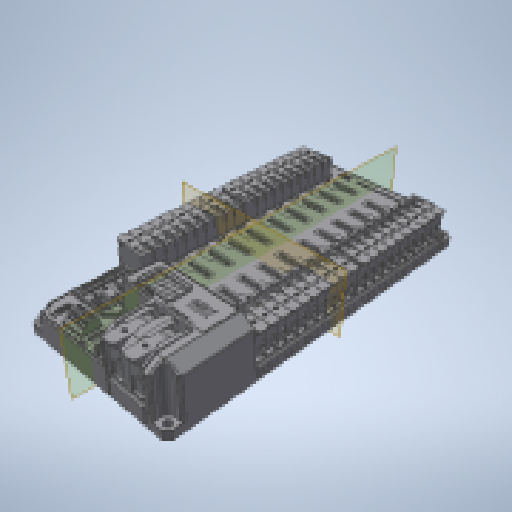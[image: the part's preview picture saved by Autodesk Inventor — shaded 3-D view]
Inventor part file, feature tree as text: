
AUTODESK INVENTOR PART (.ipt)
format: ipt  version: 2023.3 (Build 273359000, 359)  size: 30,591,488 bytes
history: native  units: mm (DEFAULTED — no unit token found)
features: other x402, plane x2
ambient origin geometry x8: Origin, YZ Plane, XZ Plane, XY Plane, X Axis, Y Axis, Z Axis, Center Point
bodies: Solid1 (feature_tree), Solid2 (feature_tree), Solid3 (feature_tree), Solid4 (feature_tree), Solid5 (feature_tree), Solid6 (feature_tree), Solid7 (feature_tree), Solid8 (feature_tree), Solid9 (feature_tree), Solid10 (feature_tree), Solid11 (feature_tree), Solid12 (feature_tree), Solid13 (feature_tree), Solid14 (feature_tree), Solid15 (feature_tree), Solid16 (feature_tree), Solid17 (feature_tree), Solid18 (feature_tree), Solid19 (feature_tree), Solid20 (feature_tree), Solid21 (feature_tree), Solid22 (feature_tree), Solid23 (feature_tree), Solid24 (feature_tree), Solid25 (feature_tree), Solid26 (feature_tree), Solid27 (feature_tree), Solid28 (feature_tree), Solid29 (feature_tree), Solid30 (feature_tree), Solid31 (feature_tree), Solid32 (feature_tree), Solid33 (feature_tree), Solid34 (feature_tree), Solid35 (feature_tree), Solid36 (feature_tree), Solid37 (feature_tree), Solid38 (feature_tree), Solid39 (feature_tree), Solid40 (feature_tree), Solid41 (feature_tree), Solid42 (feature_tree), Solid43 (feature_tree), Solid44 (feature_tree), Solid45 (feature_tree), Solid46 (feature_tree), Solid47 (feature_tree), Solid48 (feature_tree), Solid49 (feature_tree), Solid50 (feature_tree), Solid51 (feature_tree), Solid52 (feature_tree), Solid53 (feature_tree), Solid54 (feature_tree), Solid55 (feature_tree), Solid56 (feature_tree), Solid57 (feature_tree), Solid58 (feature_tree), Solid59 (feature_tree), Solid60 (feature_tree), Solid61 (feature_tree), Solid62 (feature_tree), Solid63 (feature_tree), Solid64 (feature_tree), Solid65 (feature_tree), Solid66 (feature_tree), Solid67 (feature_tree), Solid68 (feature_tree), Solid69 (feature_tree), Solid70 (feature_tree), Solid71 (feature_tree), Solid72 (feature_tree), Solid73 (feature_tree), Solid74 (feature_tree), Solid75 (feature_tree), Solid76 (feature_tree), Solid77 (feature_tree), Solid78 (feature_tree), Solid79 (feature_tree), Solid80 (feature_tree), Solid81 (feature_tree), Solid82 (feature_tree), Solid83 (feature_tree), Solid84 (feature_tree), Solid85 (feature_tree), Solid86 (feature_tree), Solid87 (feature_tree), Solid88 (feature_tree), Solid89 (feature_tree), Solid90 (feature_tree), Solid91 (feature_tree), Solid92 (feature_tree), Solid93 (feature_tree), Solid94 (feature_tree), Solid95 (feature_tree), Solid96 (feature_tree), Solid97 (feature_tree), Solid98 (feature_tree), Solid99 (feature_tree), Solid100 (feature_tree), Solid101 (feature_tree), Solid102 (feature_tree), Solid103 (feature_tree), Solid104 (feature_tree), Solid105 (feature_tree), Solid106 (feature_tree), Solid107 (feature_tree), Solid108 (feature_tree), Solid109 (feature_tree), Solid110 (feature_tree), Solid111 (feature_tree), Solid112 (feature_tree), Solid113 (feature_tree), Solid114 (feature_tree), Solid115 (feature_tree), Solid116 (feature_tree), Solid117 (feature_tree), Solid118 (feature_tree), Solid119 (feature_tree), Solid120 (feature_tree), Solid121 (feature_tree), Solid122 (feature_tree), Solid123 (feature_tree), Solid124 (feature_tree), Solid125 (feature_tree), Solid126 (feature_tree), Solid127 (feature_tree), Solid128 (feature_tree), Solid129 (feature_tree), Solid130 (feature_tree), Solid131 (feature_tree), Solid132 (feature_tree), Solid133 (feature_tree), Solid134 (feature_tree), Solid135 (feature_tree), Solid136 (feature_tree), Solid137 (feature_tree), Solid138 (feature_tree), Solid139 (feature_tree), Solid140 (feature_tree), Solid141 (feature_tree), Solid142 (feature_tree), Solid143 (feature_tree), Solid144 (feature_tree), Solid145 (feature_tree), Solid146 (feature_tree), Solid147 (feature_tree), Solid148 (feature_tree), Solid149 (feature_tree), Solid150 (feature_tree), Solid151 (feature_tree), Solid152 (feature_tree), Solid153 (feature_tree), Solid154 (feature_tree), Solid155 (feature_tree), Solid156 (feature_tree), Solid157 (feature_tree), Solid158 (feature_tree), Solid159 (feature_tree), Solid160 (feature_tree), Solid161 (feature_tree), Solid162 (feature_tree), Solid163 (feature_tree), Solid164 (feature_tree), Solid165 (feature_tree), Solid166 (feature_tree), Solid167 (feature_tree), Solid168 (feature_tree), Solid169 (feature_tree), Solid170 (feature_tree), Solid171 (feature_tree), Solid172 (feature_tree), Solid173 (feature_tree), Solid174 (feature_tree), Solid175 (feature_tree), Solid176 (feature_tree), Solid177 (feature_tree), Solid178 (feature_tree), Solid179 (feature_tree), Solid180 (feature_tree), Solid181 (feature_tree), Solid182 (feature_tree), Solid183 (feature_tree), Solid184 (feature_tree), Solid185 (feature_tree), Solid186 (feature_tree), Solid187 (feature_tree), Solid188 (feature_tree), Solid189 (feature_tree), Solid190 (feature_tree), Solid191 (feature_tree), Solid192 (feature_tree), Solid193 (feature_tree), Solid194 (feature_tree), Solid195 (feature_tree), Solid196 (feature_tree), Solid197 (feature_tree), Solid198 (feature_tree), Solid199 (feature_tree), Solid200 (feature_tree), Solid201 (feature_tree), Solid202 (feature_tree), Solid203 (feature_tree), Solid204 (feature_tree), Solid205 (feature_tree), Solid206 (feature_tree), Solid207 (feature_tree), Solid208 (feature_tree), Solid209 (feature_tree), Solid210 (feature_tree), Solid211 (feature_tree), Solid212 (feature_tree), Solid213 (feature_tree), Solid214 (feature_tree), Solid215 (feature_tree), Solid216 (feature_tree), Solid217 (feature_tree), Solid218 (feature_tree), Solid219 (feature_tree), Solid220 (feature_tree), Solid221 (feature_tree), Solid222 (feature_tree), Solid223 (feature_tree), Solid224 (feature_tree), Solid225 (feature_tree), Solid226 (feature_tree), Solid227 (feature_tree), Solid228 (feature_tree), Solid229 (feature_tree), Solid230 (feature_tree), Solid231 (feature_tree), Solid232 (feature_tree), Solid233 (feature_tree), Solid234 (feature_tree), Solid235 (feature_tree), Solid236 (feature_tree), Solid237 (feature_tree), Solid238 (feature_tree), Solid239 (feature_tree), Solid240 (feature_tree), Solid241 (feature_tree), Solid242 (feature_tree), Solid243 (feature_tree), Solid244 (feature_tree), Solid245 (feature_tree), Solid246 (feature_tree), Solid247 (feature_tree), Solid248 (feature_tree), Solid249 (feature_tree), Solid250 (feature_tree), Solid251 (feature_tree), Solid252 (feature_tree), Solid253 (feature_tree), Solid254 (feature_tree), Solid255 (feature_tree), Solid256 (feature_tree), Solid257 (feature_tree), Solid258 (feature_tree), Solid259 (feature_tree), Solid260 (feature_tree), Solid261 (feature_tree), Solid262 (feature_tree), Solid263 (feature_tree), Solid264 (feature_tree), Solid265 (feature_tree), Solid266 (feature_tree), Solid267 (feature_tree), Solid268 (feature_tree), Solid269 (feature_tree), Solid270 (feature_tree), Solid271 (feature_tree), Solid272 (feature_tree), Solid273 (feature_tree), Solid274 (feature_tree), Solid275 (feature_tree), Solid276 (feature_tree), Solid277 (feature_tree), Solid278 (feature_tree), Solid279 (feature_tree), Solid280 (feature_tree), Solid281 (feature_tree), Solid282 (feature_tree), Solid283 (feature_tree), Solid284 (feature_tree), Solid285 (feature_tree), Solid286 (feature_tree), Solid287 (feature_tree), Solid288 (feature_tree), Solid289 (feature_tree), Solid290 (feature_tree), Solid291 (feature_tree), Solid292 (feature_tree), Solid293 (feature_tree), Solid294 (feature_tree), Solid295 (feature_tree), Solid296 (feature_tree), Solid297 (feature_tree), Solid298 (feature_tree), Solid299 (feature_tree), Solid300 (feature_tree), Solid301 (feature_tree), Solid302 (feature_tree), Solid303 (feature_tree), Solid304 (feature_tree), Solid305 (feature_tree), Solid306 (feature_tree), Solid307 (feature_tree), Solid308 (feature_tree), Solid309 (feature_tree), Solid310 (feature_tree), Solid311 (feature_tree), Solid312 (feature_tree), Solid313 (feature_tree), Solid314 (feature_tree), Solid315 (feature_tree), Solid316 (feature_tree), Solid317 (feature_tree), Solid318 (feature_tree), Solid319 (feature_tree), Solid320 (feature_tree), Solid321 (feature_tree), Solid322 (feature_tree), Solid323 (feature_tree), Solid324 (feature_tree), Solid325 (feature_tree), Solid326 (feature_tree), Solid327 (feature_tree), Solid328 (feature_tree), Solid329 (feature_tree), Solid330 (feature_tree), Solid331 (feature_tree), Solid332 (feature_tree), Solid333 (feature_tree), Solid334 (feature_tree), Solid335 (feature_tree), Solid336 (feature_tree), Solid337 (feature_tree), Solid338 (feature_tree), Solid339 (feature_tree), Solid340 (feature_tree), Solid341 (feature_tree), Solid342 (feature_tree), Solid343 (feature_tree), Solid344 (feature_tree), Solid345 (feature_tree), Solid346 (feature_tree), Solid347 (feature_tree), Solid348 (feature_tree), Solid349 (feature_tree), Solid350 (feature_tree), Solid351 (feature_tree), Solid352 (feature_tree), Solid353 (feature_tree), Solid354 (feature_tree), Solid355 (feature_tree), Solid356 (feature_tree), Solid357 (feature_tree), Solid358 (feature_tree), Solid359 (feature_tree), Solid360 (feature_tree), Solid361 (feature_tree), Solid362 (feature_tree), Solid363 (feature_tree), Solid364 (feature_tree), Solid365 (feature_tree), Solid366 (feature_tree), Solid367 (feature_tree), Solid368 (feature_tree), Solid369 (feature_tree), Solid370 (feature_tree), Solid371 (feature_tree), Solid372 (feature_tree), Solid373 (feature_tree), Solid374 (feature_tree), Solid375 (feature_tree), Solid376 (feature_tree), Solid377 (feature_tree), Solid378 (feature_tree), Solid379 (feature_tree), Solid380 (feature_tree), Solid381 (feature_tree), Solid382 (feature_tree), Solid383 (feature_tree), Solid384 (feature_tree), Solid385 (feature_tree), Solid386 (feature_tree), Solid387 (feature_tree), Solid388 (feature_tree), Solid389 (feature_tree), Solid390 (feature_tree), Solid391 (feature_tree), Solid392 (feature_tree), Solid393 (feature_tree), Solid394 (feature_tree), Solid395 (feature_tree), Solid396 (feature_tree), Solid397 (feature_tree), Solid398 (feature_tree), Solid399 (feature_tree), Solid400 (feature_tree), Solid401 (feature_tree), Solid402 (feature_tree), Solid403 (feature_tree)
feature tree (404):
  plane  "Work Plane1"
  plane  "Work Plane2"
  other  "REV-11-1850-P01-1-solid1"
  other  "REV-11-1850-P02-1-solid1"
  other  "REV-11-1850-P02-1-solid2"
  other  "REV-11-1850-P02-1-solid3"
  other  "REV-11-1850-P02-1-solid4"
  other  "REV-11-1850-P02-1-solid5"
  other  "REV-11-1850-P02-1-solid6"
  other  "REV-11-1850-P02-1-solid7"
  other  "REV-11-1850-P02-1-solid8"
  other  "REV-11-1850-P02-1-solid9"
  other  "REV-11-1850-P02-1-solid10"
  other  "REV-11-1850-P02-1-solid11"
  other  "REV-11-1850-P02-1-solid12"
  other  "REV-11-1850-P02-1-solid13"
  other  "REV-11-1850-P02-1-solid14"
  other  "REV-11-1850-P02-1-solid15"
  other  "REV-11-1850-P02-1-solid16"
  other  "REV-11-1850-P02-1-solid17"
  other  "REV-11-1850-P02-1-solid18"
  other  "REV-11-1850-P02-1-solid19"
  other  "REV-11-1850-P02-1-solid20"
  other  "REV-11-1850-P02-1-solid21"
  other  "REV-11-1850-P02-1-solid22"
  other  "REV-11-1850-P02-1-solid23"
  other  "REV-11-1850-P02-1-solid24"
  other  "REV-11-1850-P02-1-solid25"
  other  "REV-11-1850-P02-1-solid26"
  other  "REV-11-1850-P02-1-solid27"
  other  "REV-11-1850-P02-1-solid28"
  other  "REV-11-1850-P02-1-solid29"
  other  "REV-11-1850-P02-1-solid30"
  other  "REV-11-1850-P02-1-solid31"
  other  "REV-11-1850-P02-1-solid32"
  other  "REV-11-1850-P02-1-solid33"
  other  "REV-11-1850-P03-1-solid1"
  other  "REV-11-1850-P03-1-solid2"
  other  "REV-11-1850-P03-1-solid3"
  other  "REV-11-1850-P03-1-solid4"
  other  "REV-11-1850-P03-1-solid5"
  other  "REV-11-1850-P03-1-solid6"
  other  "REV-11-1850-P03-1-solid7"
  other  "REV-11-1850-P03-1-solid8"
  other  "REV-11-1850-P03-1-solid9"
  other  "REV-11-1850-P03-1-solid10"
  other  "REV-11-1850-P03-1-solid11"
  other  "REV-11-1850-P03-1-solid12"
  other  "REV-11-1850-P03-1-solid13"
  other  "REV-11-1850-P03-1-solid14"
  other  "REV-11-1850-P03-1-solid15"
  other  "REV-11-1850-P03-1-solid16"
  other  "REV-11-1850-P03-1-solid17"
  other  "REV-11-1850-P03-1-solid18"
  other  "REV-11-1850-P03-1-solid19"
  other  "REV-11-1850-P03-1-solid20"
  other  "REV-11-1850-P03-1-solid21"
  other  "REV-11-1850-P03-1-solid22"
  other  "REV-11-1850-P03-1-solid23"
  other  "REV-11-1850-P03-1-solid24"
  other  "REV-11-1850-P03-1-solid25"
  other  "REV-11-1850-P03-1-solid26"
  other  "REV-11-1850-P03-1-solid27"
  other  "REV-11-1850-P03-1-solid28"
  other  "REV-11-1850-P03-1-solid29"
  other  "REV-11-1850-P03-1-solid30"
  other  "REV-11-1850-P03-1-solid31"
  other  "REV-11-1850-P03-1-solid32"
  other  "REV-11-1850-P03-1-solid33"
  other  "REV-11-1850-P03-1-solid34"
  other  "REV-11-1850-P03-1-solid35"
  other  "REV-11-1850-P03-1-solid36"
  other  "REV-11-1850-P03-1-solid37"
  other  "REV-11-1850-P03-1-solid38"
  other  "REV-11-1850-P03-1-solid39"
  other  "REV-11-1850-P03-1-solid40"
  other  "REV-11-1850-P04-1-solid1"
  other  "REV-11-1850-P04-1-solid2"
  other  "REV-11-1850-P04-1-solid3"
  other  "REV-11-1850-P04-1-solid4"
  other  "REV-11-1850-P04-1-solid5"
  other  "REV-11-1850-P04-1-solid6"
  other  "REV-11-1850-P04-1-solid7"
  other  "REV-11-1850-P04-1-solid8"
  other  "REV-11-1850-P04-1-solid9"
  other  "REV-11-1850-P04-1-solid10"
  other  "REV-11-1850-P04-1-solid11"
  other  "REV-11-1850-P04-1-solid12"
  other  "REV-11-1850-P04-1-solid13"
  other  "REV-11-1850-P04-1-solid14"
  other  "REV-11-1850-P04-1-solid15"
  other  "REV-11-1850-P04-1-solid16"
  other  "REV-11-1850-P04-1-solid17"
  other  "REV-11-1850-P04-1-solid18"
  other  "REV-11-1850-P04-1-solid19"
  other  "REV-11-1850-P04-1-solid20"
  other  "REV-11-1850-P04-1-solid21"
  other  "REV-11-1850-P04-1-solid22"
  other  "REV-11-1850-P04-1-solid23"
  other  "REV-11-1850-P04-1-solid24"
  other  "REV-11-1850-P04-1-solid25"
  other  "REV-11-1850-P04-1-solid26"
  other  "REV-11-1850-P04-1-solid27"
  other  "REV-11-1850-P04-1-solid28"
  other  "REV-11-1850-P04-1-solid29"
  other  "REV-11-1850-P04-1-solid30"
  other  "REV-11-1850-P04-1-solid31"
  other  "REV-11-1850-P04-1-solid32"
  other  "REV-11-1850-P04-1-solid33"
  other  "REV-11-1850-P04-1-solid34"
  other  "REV-11-1850-P04-1-solid35"
  other  "REV-11-1850-P04-1-solid36"
  other  "REV-11-1850-P04-1-solid37"
  other  "REV-11-1850-P04-1-solid38"
  other  "REV-11-1850-P04-1-solid39"
  other  "REV-11-1850-P04-1-solid40"
  other  "REV-11-1850-P04-1-solid41"
  other  "REV-11-1850-P04-1-solid42"
  other  "REV-11-1850-P04-1-solid43"
  other  "REV-11-1850-P04-1-solid44"
  other  "REV-11-1850-P04-1-solid45"
  other  "REV-11-1850-P04-1-solid46"
  other  "REV-11-1850-P04-1-solid47"
  other  "REV-11-1850-P04-1-solid48"
  other  "REV-11-1850-P04-1-solid49"
  other  "REV-11-1850-P04-1-solid50"
  other  "REV-11-1850-P04-1-solid51"
  other  "REV-11-1850-P04-1-solid52"
  other  "REV-11-1850-P04-1-solid53"
  other  "REV-11-1850-P04-1-solid54"
  other  "REV-11-1850-P04-1-solid55"
  other  "REV-11-1850-P04-1-solid56"
  other  "REV-11-1850-P04-1-solid57"
  other  "REV-11-1850-P04-1-solid58"
  other  "REV-11-1850-P04-1-solid59"
  other  "REV-11-1850-P04-1-solid60"
  other  "REV-11-1850-P04-1-solid61"
  other  "REV-11-1850-P04-1-solid62"
  other  "REV-11-1850-P04-1-solid63"
  other  "REV-11-1850-P04-1-solid64"
  other  "REV-11-1850-P04-1-solid65"
  other  "REV-11-1850-P04-1-solid66"
  other  "REV-11-1850-P04-1-solid67"
  other  "REV-11-1850-P04-1-solid68"
  other  "REV-11-1850-P04-1-solid69"
  other  "REV-11-1850-P04-1-solid70"
  other  "REV-11-1850-P04-1-solid71"
  other  "REV-11-1850-P04-1-solid72"
  other  "REV-11-1850-P04-1-solid73"
  other  "REV-11-1850-P04-1-solid74"
  other  "REV-11-1850-P04-1-solid75"
  other  "REV-11-1850-P04-1-solid76"
  other  "REV-11-1850-P04-1-solid77"
  other  "REV-11-1850-P04-1-solid78"
  other  "REV-11-1850-P04-1-solid79"
  other  "REV-11-1850-P04-1-solid80"
  other  "REV-11-1850-P04-1-solid81"
  other  "REV-11-1850-P04-1-solid82"
  other  "REV-11-1850-P04-1-solid83"
  other  "REV-11-1850-P04-1-solid84"
  other  "REV-11-1850-P04-1-solid85"
  other  "REV-11-1850-P04-1-solid86"
  other  "REV-11-1850-P04-1-solid87"
  other  "REV-11-1850-P04-1-solid88"
  other  "REV-11-1850-P04-1-solid89"
  other  "REV-11-1850-P04-1-solid90"
  other  "REV-11-1850-P04-1-solid91"
  other  "REV-11-1850-P04-1-solid92"
  other  "REV-11-1850-P04-1-solid93"
  other  "REV-11-1850-P04-1-solid94"
  other  "REV-11-1850-P04-1-solid95"
  other  "REV-11-1850-P04-1-solid96"
  other  "REV-11-1850-P04-1-solid97"
  other  "REV-11-1850-P04-1-solid98"
  other  "REV-11-1850-P04-1-solid99"
  other  "REV-11-1850-P04-1-solid100"
  other  "REV-11-1850-P04-1-solid101"
  other  "REV-11-1850-P04-1-solid102"
  other  "REV-11-1850-P04-1-solid103"
  other  "REV-11-1850-P04-1-solid104"
  other  "REV-11-1850-P04-1-solid105"
  other  "REV-11-1850-P04-1-solid106"
  other  "REV-11-1850-P04-1-solid107"
  other  "REV-11-1850-P05-1-solid1"
  other  "REV-11-1850-P05-1-solid2"
  other  "REV-11-1850-P05-1-solid3"
  other  "REV-11-1850-P05-1-solid4"
  other  "REV-11-1850-P05-1-solid5"
  other  "REV-11-1850-P05-1-solid6"
  other  "REV-11-1850-P05-1-solid7"
  other  "REV-11-1850-P05-1-solid8"
  other  "REV-11-1850-P05-1-solid9"
  other  "REV-11-1850-P05-1-solid10"
  other  "REV-11-1850-P05-1-solid11"
  other  "REV-11-1850-P05-1-solid12"
  other  "REV-11-1850-P05-1-solid13"
  other  "REV-11-1850-P05-1-solid14"
  other  "REV-11-1850-P05-1-solid15"
  other  "REV-11-1850-P05-1-solid16"
  other  "REV-11-1850-P05-1-solid17"
  other  "REV-11-1850-P05-1-solid18"
  other  "REV-11-1850-P05-1-solid19"
  other  "REV-11-1850-P05-1-solid20"
  other  "REV-11-1850-P05-1-solid21"
  other  "REV-11-1850-P05-1-solid22"
  other  "REV-11-1850-P05-1-solid23"
  other  "REV-11-1850-P05-1-solid24"
  other  "REV-11-1850-P05-1-solid25"
  other  "REV-11-1850-P05-1-solid26"
  other  "REV-11-1850-P05-1-solid27"
  other  "REV-11-1850-P05-1-solid28"
  other  "REV-11-1850-P05-1-solid29"
  other  "REV-11-1850-P05-1-solid30"
  other  "REV-11-1850-P05-1-solid31"
  other  "REV-11-1850-P05-1-solid32"
  other  "REV-11-1850-P05-1-solid33"
  other  "REV-11-1850-P05-1-solid34"
  other  "REV-11-1850-P05-1-solid35"
  other  "REV-11-1850-P05-1-solid36"
  other  "REV-11-1850-P06-1-solid1"
  other  "VOLTMETER DISPLAY-1-solid1"
  other  "VOLTMETER DISPLAY-1-solid2"
  other  "VOLTMETER DISPLAY-1-solid3"
  other  "M2X6 THREAD FORMING SCREW-1-solid1"
  other  "M2X6 THREAD FORMING SCREW-1-solid2"
  other  "M2X6 THREAD FORMING SCREW-3-solid1"
  other  "M2X6 THREAD FORMING SCREW-3-solid2"
  other  "M2X6 THREAD FORMING SCREW-4-solid1"
  other  "M2X6 THREAD FORMING SCREW-4-solid2"
  other  "M2X6 THREAD FORMING SCREW-5-solid1"
  other  "M2X6 THREAD FORMING SCREW-5-solid2"
  other  "M2X6 THREAD FORMING SCREW-6-solid1"
  other  "M2X6 THREAD FORMING SCREW-6-solid2"
  other  "M2X6 THREAD FORMING SCREW-7-solid1"
  other  "M2X6 THREAD FORMING SCREW-7-solid2"
  other  "M3X8 THREAD FORMING SCREW-1-solid1"
  other  "M3X8 THREAD FORMING SCREW-1-solid2"
  other  "M3X8 THREAD FORMING SCREW-2-solid1"
  other  "M3X8 THREAD FORMING SCREW-2-solid2"
  other  "M3X8 THREAD FORMING SCREW-3-solid1"
  other  "M3X8 THREAD FORMING SCREW-3-solid2"
  other  "M3X8 THREAD FORMING SCREW-4-solid1"
  other  "M3X8 THREAD FORMING SCREW-4-solid2"
  other  "REV-11-1850-F-CTL-1_REV-11-1850-F-CTL-1-solid1"
  other  "REV-11-1850-F-CTL-1_WAGO CAN 4-POLE BLOCK-01"
  other  "REV-11-1850-F-CTL-1_WAGO CAN 4-POLE BLOCK-02"
  other  "REV-11-1850-F-CTL-1_WAGO CAN 4-POLE BLOCK-03"
  other  "REV-11-1850-F-CTL-1_WAGO CAN 4-POLE BLOCK-04"
  other  "REV-11-1850-F-CTL-1_WAGO CAN 4-POLE BLOCK-05"
  other  "REV-11-1850-F-CTL-1_SWITCH-1-solid1"
  parser-record x1  (decoder bookkeeping rows leaked as tree rows — omitted from the tree; the rows remain in map.json)
  other  "NONE:1"
  other  "REV-11-1850-F-CTL-1_Low Profile Tack Switch-1-solid1"
  other  "REV-11-1850-F-CTL-1_LED-01"
  other  "REV-11-1850-F-PWR-1_REV-11-1850-F-PWR-1-solid1"
  other  "REV-11-1850-F-PWR-1_WAGO-01"
  other  "REV-11-1850-F-PWR-1_WAGO-02"
  other  "REV-11-1850-F-PWR-1_WAGO-03"
  other  "REV-11-1850-F-PWR-1_WAGO-04"
  other  "REV-11-1850-F-PWR-1_WAGO-05"
  other  "REV-11-1850-F-PWR-1_WAGO-06"
  other  "REV-11-1850-F-PWR-1_WAGO-07"
  other  "REV-11-1850-F-PWR-1_WAGO-08"
  other  "REV-11-1850-F-PWR-1_WAGO-09"
  other  "REV-11-1850-F-PWR-1_WAGO-10"
  other  "REV-11-1850-F-PWR-1_WAGO-11"
  other  "REV-11-1850-F-PWR-1_WAGO-12"
  other  "REV-11-1850-F-PWR-1_WAGO-13"
  other  "REV-11-1850-F-PWR-1_WAGO-14"
  other  "REV-11-1850-F-PWR-1_WAGO-15"
  other  "REV-11-1850-F-PWR-1_WAGO-16"
  other  "REV-11-1850-F-PWR-1_WAGO-17"
  other  "REV-11-1850-F-PWR-1_WAGO-18"
  other  "REV-11-1850-F-PWR-1_WAGO-19"
  other  "REV-11-1850-F-PWR-1_WAGO-20"
  other  "REV-11-1850-F-PWR-1_WAGO-21"
  other  "REV-11-1850-F-PWR-1_WAGO-22"
  other  "REV-11-1850-F-PWR-1_WAGO-23"
  other  "REV-11-1850-F-PWR-1_WAGO-24"
  other  "REV-11-1850-F-PWR-1_WAGO-25"
  other  "REV-11-1850-F-PWR-1_WAGO-26"
  other  "REV-11-1850-F-PWR-1_WAGO-27"
  other  "REV-11-1850-F-PWR-1_WAGO-28"
  other  "REV-11-1850-F-PWR-1_WAGO-29"
  other  "REV-11-1850-F-PWR-1_WAGO-30"
  other  "REV-11-1850-F-PWR-1_WAGO-31"
  other  "REV-11-1850-F-PWR-1_WAGO-32"
  other  "REV-11-1850-F-PWR-1_WAGO-33"
  other  "REV-11-1850-F-PWR-1_WAGO-34"
  other  "REV-11-1850-F-PWR-1_WAGO-35"
  other  "REV-11-1850-F-PWR-1_WAGO-36"
  other  "REV-11-1850-F-PWR-1_WAGO-37"
  other  "REV-11-1850-F-PWR-1_WAGO-38"
  other  "REV-11-1850-F-PWR-1_WAGO-39"
  other  "REV-11-1850-F-PWR-1_WAGO-40"
  other  "REV-11-1850-F-PWR-1_2 POLE WAGO INPUT-01"
  other  "REV-11-1850-F-PWR-1_2 POLE WAGO INPUT-02"
  other  "REV-11-1850-F-PWR-1_2 POLE WAGO INPUT-03"
  other  "REV-11-1850-F-PWR-1_2 POLE WAGO INPUT-04"
  other  "REV-11-1850-F-PWR-1_8 POLE WAGO POWER BLOCK OUTPUT-1_SPACER BLACK-1-solid1"
  other  "REV-11-1850-F-PWR-1_8 POLE WAGO POWER BLOCK OUTPUT-1_BLACK POLE-5-solid1"
  other  "REV-11-1850-F-PWR-1_8 POLE WAGO POWER BLOCK OUTPUT-1_RED POLE-5-solid1"
  other  "REV-11-1850-F-PWR-1_8 POLE WAGO POWER BLOCK OUTPUT-1_RED POLE-6-solid1"
  other  "REV-11-1850-F-PWR-1_8 POLE WAGO POWER BLOCK OUTPUT-1_RED POLE-7-solid1"
  other  "REV-11-1850-F-PWR-1_8 POLE WAGO POWER BLOCK OUTPUT-1_RED POLE-8-solid1"
  other  "REV-11-1850-F-PWR-1_8 POLE WAGO POWER BLOCK OUTPUT-1_BLACK POLE-7-solid1"
  other  "REV-11-1850-F-PWR-1_8 POLE WAGO POWER BLOCK OUTPUT-1_BLACK POLE-8-solid1"
  other  "REV-11-1850-F-PWR-1_8 POLE WAGO POWER BLOCK OUTPUT-1_BLACK POLE-9-solid1"
  other  "NONE:2"
  other  "REV-11-1850-F-PWR-1_SBH-02"
  other  "REV-11-1850-F-PWR-1_SBH-04"
  other  "NONE:3"
  other  "REV-11-1850-F-PWR-1_SBH-06"
  other  "REV-11-1850-F-PWR-1_SBH-07"
  other  "NONE:4"
  other  "REV-11-1850-F-PWR-1_SBH-09"
  other  "REV-11-1850-F-PWR-1_SBH-10"
  other  "NONE:5"
  other  "REV-11-1850-F-PWR-1_SBH-12"
  other  "REV-11-1850-F-PWR-1_SBH-13"
  other  "NONE:6"
  other  "REV-11-1850-F-PWR-1_LBH-02"
  other  "REV-11-1850-F-PWR-1_LBH-03"
  other  "NONE:7"
  other  "REV-11-1850-F-PWR-1_LBH-05"
  other  "REV-11-1850-F-PWR-1_LBH-06"
  other  "REV-11-1850-F-PWR-1_0606 LED-1-solid1"
  other  "REV-11-1850-F-PWR-1_0606 LED-2-solid1"
  other  "REV-11-1850-F-PWR-1_0606 LED-3-solid1"
  other  "REV-11-1850-F-PWR-1_0606 LED-4-solid1"
  other  "REV-11-1850-F-PWR-1_0606 LED-5-solid1"
  other  "REV-11-1850-F-PWR-1_0606 LED-6-solid1"
  other  "REV-11-1850-F-PWR-1_0606 LED-7-solid1"
  other  "REV-11-1850-F-PWR-1_0606 LED-8-solid1"
  other  "REV-11-1850-F-PWR-1_0606 LED-9-solid1"
  other  "REV-11-1850-F-PWR-1_0606 LED-10-solid1"
  other  "NONE:8"
  other  "REV-11-1850-F-PWR-1_LBH-08"
  other  "REV-11-1850-F-PWR-1_LBH-09"
  other  "NONE:9"
  other  "REV-11-1850-F-PWR-1_LBH-11"
  other  "REV-11-1850-F-PWR-1_LBH-12"
  other  "NONE:10"
  other  "REV-11-1850-F-PWR-1_LBH-14"
  other  "REV-11-1850-F-PWR-1_LBH-15"
  other  "NONE:11"
  other  "REV-11-1850-F-PWR-1_LBH-17"
  other  "REV-11-1850-F-PWR-1_LBH-18"
  other  "NONE:12"
  other  "REV-11-1850-F-PWR-1_LBH-20"
  other  "REV-11-1850-F-PWR-1_LBH-21"
  other  "NONE:13"
  other  "REV-11-1850-F-PWR-1_LBH-23"
  other  "REV-11-1850-F-PWR-1_LBH-24"
  other  "NONE:14"
  other  "REV-11-1850-F-PWR-1_LBH-26"
  other  "REV-11-1850-F-PWR-1_LBH-27"
  other  "NONE:15"
  other  "REV-11-1850-F-PWR-1_LBH-29"
  other  "REV-11-1850-F-PWR-1_LBH-30"
  other  "REV-11-1850-F-PWR-1_0606 LED-11-solid1"
  other  "REV-11-1850-F-PWR-1_0606 LED-12-solid1"
  other  "NONE:16"
  other  "REV-11-1850-F-PWR-1_LBH-32"
  other  "REV-11-1850-F-PWR-1_LBH-33"
  other  "NONE:17"
  other  "REV-11-1850-F-PWR-1_LBH-35"
  other  "REV-11-1850-F-PWR-1_LBH-36"
  other  "REV-11-1850-F-PWR-1_0606 LED-13-solid1"
  other  "REV-11-1850-F-PWR-1_0606 LED-14-solid1"
  other  "REV-11-1850-F-PWR-1_0606 LED-15-solid1"
  other  "REV-11-1850-F-PWR-1_0606 LED-16-solid1"
  other  "REV-11-1850-F-PWR-1_0606 LED-17-solid1"
  other  "REV-11-1850-F-PWR-1_0606 LED-18-solid1"
  other  "REV-11-1850-F-PWR-1_0606 LED-19-solid1"
  other  "REV-11-1850-F-PWR-1_0606 LED-20-solid1"
  other  "NONE:18"
  other  "REV-11-1850-F-PWR-1_LBH-38"
  other  "REV-11-1850-F-PWR-1_LBH-39"
  other  "NONE:19"
  other  "REV-11-1850-F-PWR-1_LBH-41"
  other  "REV-11-1850-F-PWR-1_LBH-42"
  other  "NONE:20"
  other  "REV-11-1850-F-PWR-1_LBH-44"
  other  "REV-11-1850-F-PWR-1_LBH-45"
  other  "NONE:21"
  other  "REV-11-1850-F-PWR-1_LBH-47"
  other  "REV-11-1850-F-PWR-1_LBH-48"
  other  "NONE:22"
  other  "REV-11-1850-F-PWR-1_LBH-50"
  other  "REV-11-1850-F-PWR-1_LBH-51"
  other  "NONE:23"
  other  "REV-11-1850-F-PWR-1_LBH-53"
  other  "REV-11-1850-F-PWR-1_LBH-54"
  other  "NONE:24"
  other  "REV-11-1850-F-PWR-1_LBH-56"
  other  "REV-11-1850-F-PWR-1_LBH-57"
  other  "NONE:25"
  other  "REV-11-1850-F-PWR-1_LBH-59"
  other  "REV-11-1850-F-PWR-1_LBH-60"
  other  "REV-11-1850-F-PWR-1_0606 LED-21-solid1"
  other  "REV-11-1850-F-PWR-1_0606 LED-22-solid1"
  other  "REV-11-1850-F-PWR-1_0606 LED-23-solid1"
  other  "REV-11-1850-F-PWR-1_0606 LED-24-solid1"
